# Revit family: Sun-Shades_MITHRA_PalmSHIELD
name_source: partatom
category: Generic Models
units: mm (PartAtom-declared; Revit-internal decimal feet)

## family parameters
Always vertical = Yes
Can host rebar = No
Cut with Voids When Loaded = No
Maintain Annotation Orientation = No
Part Type = Normal
Room Calculation Point = No
Round Connector Dimension = Use Diameter
Shared = No
Work Plane-Based = No

## types (1)
- ALUMINUM PURLINS 1" x 4"
    C2 = 12' - 7 3/4"
    CAD Details = https://www.arcat.com
    Center of Center = 0' - 3"
    Default Elevation = 0' - 0"
    Finish = PalmSHIELD - Aluminum
    Keynote = 06 87 00
    Manufacturer = PalmSHIELD
    Product Page URL = https://www.arcat.com
    Purlin Height = 0' - 4"
    Purlin Width = 0' - 1"
    Specification = https://www.arcat.com
    URL = https://palmshieldlouvers.com
    Vertical Beams_Center of Center = 0' - 2"

## geometry (parser evidence)
native form markers: Sweep x10
no freeform markers — native parametric forms only
